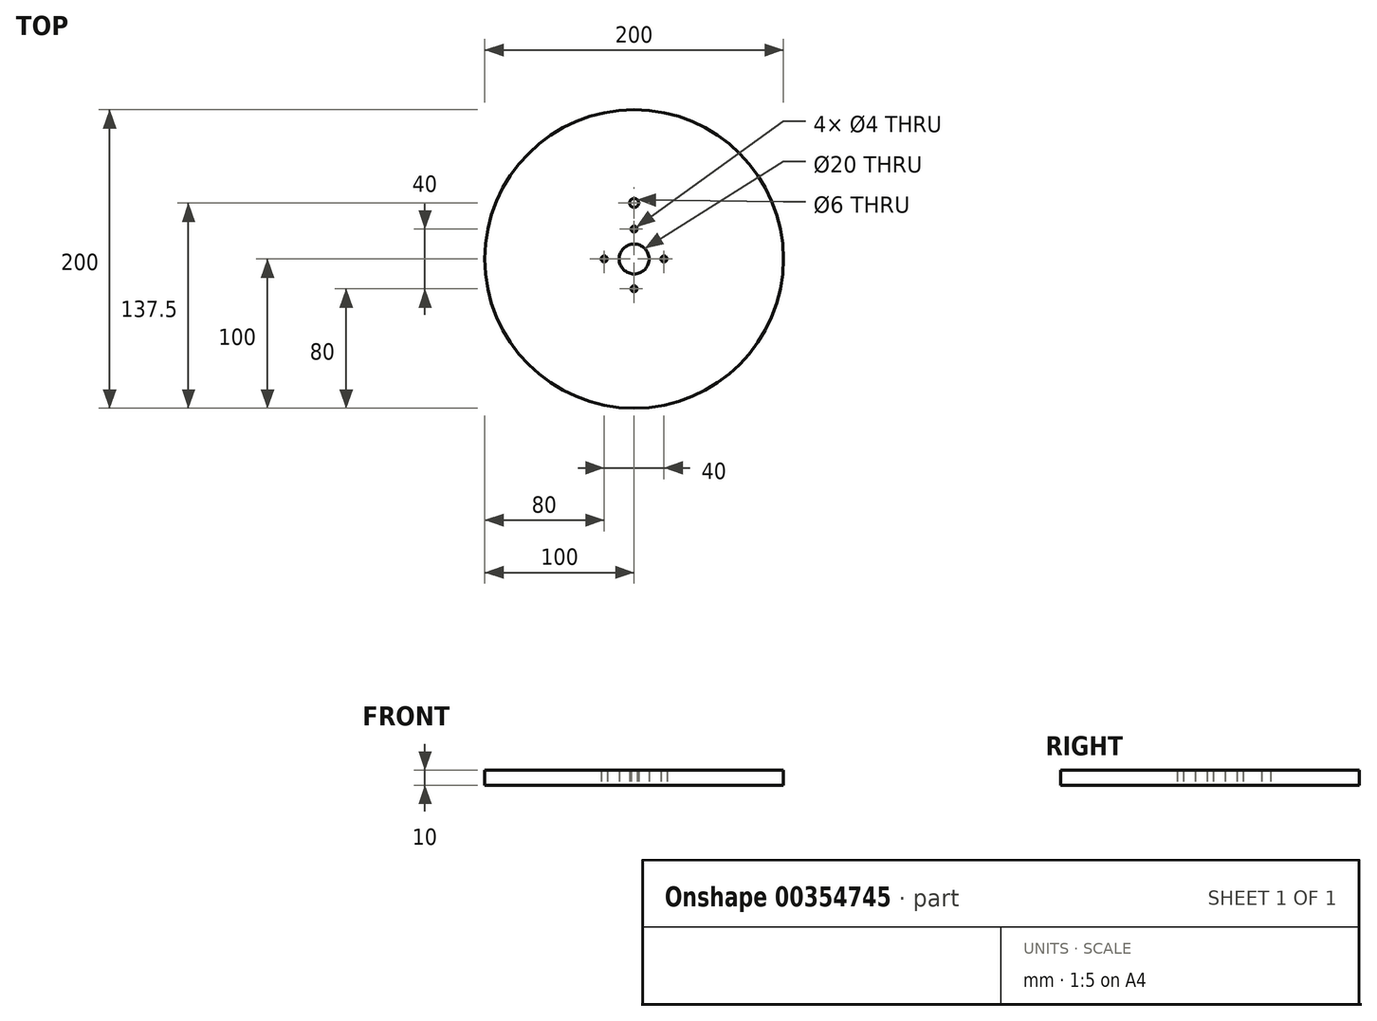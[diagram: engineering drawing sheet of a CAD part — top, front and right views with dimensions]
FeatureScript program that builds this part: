
annotation { "Feature Type Name" : "Feature", "Feature Type Description" : "" }
export const myFeature = defineFeature(function(context is Context, id is Id, definition is map)
    precondition{}
    {
        {
            var Q0;
            Q0=qCreatedBy(makeId("Top.planeOp"),FACE);
            var sketch = newSketch(context, id + "F0", { "sketchPlane" : qUnion([Q0])});
            skCircle(sketch, "E0", {"center": v(0, 0) * mm, "radius": 100 * mm});
            skCircle(sketch, "E1", {"center": v(0, 0) * mm, "radius": 10 * mm});
            skLineSegment(sketch, "E2", {"start": v(0, 0) * mm, "end": v(0, 37.5) * mm});
            skCircle(sketch, "E3", {"center": v(0, 37.5) * mm, "radius": 3 * mm});
            skCircle(sketch, "E4", {"center": v(0, 20) * mm, "radius": 2 * mm});
            skCircle(sketch, "E5", {"center": v(20, 0) * mm, "radius": 2 * mm});
            skCircle(sketch, "E6", {"center": v(0, -20) * mm, "radius": 2 * mm});
            skCircle(sketch, "E7", {"center": v(-20, 0) * mm, "radius": 2 * mm});
            skSolve(sketch);
        }
        {
            var Q0;
            Q0 = qSketchRegion(id + "F0", true);
            extrude(context, id + "F1", {"entities" : qUnion([Q0]), "depth" : 10 * mm});
        }
    });
